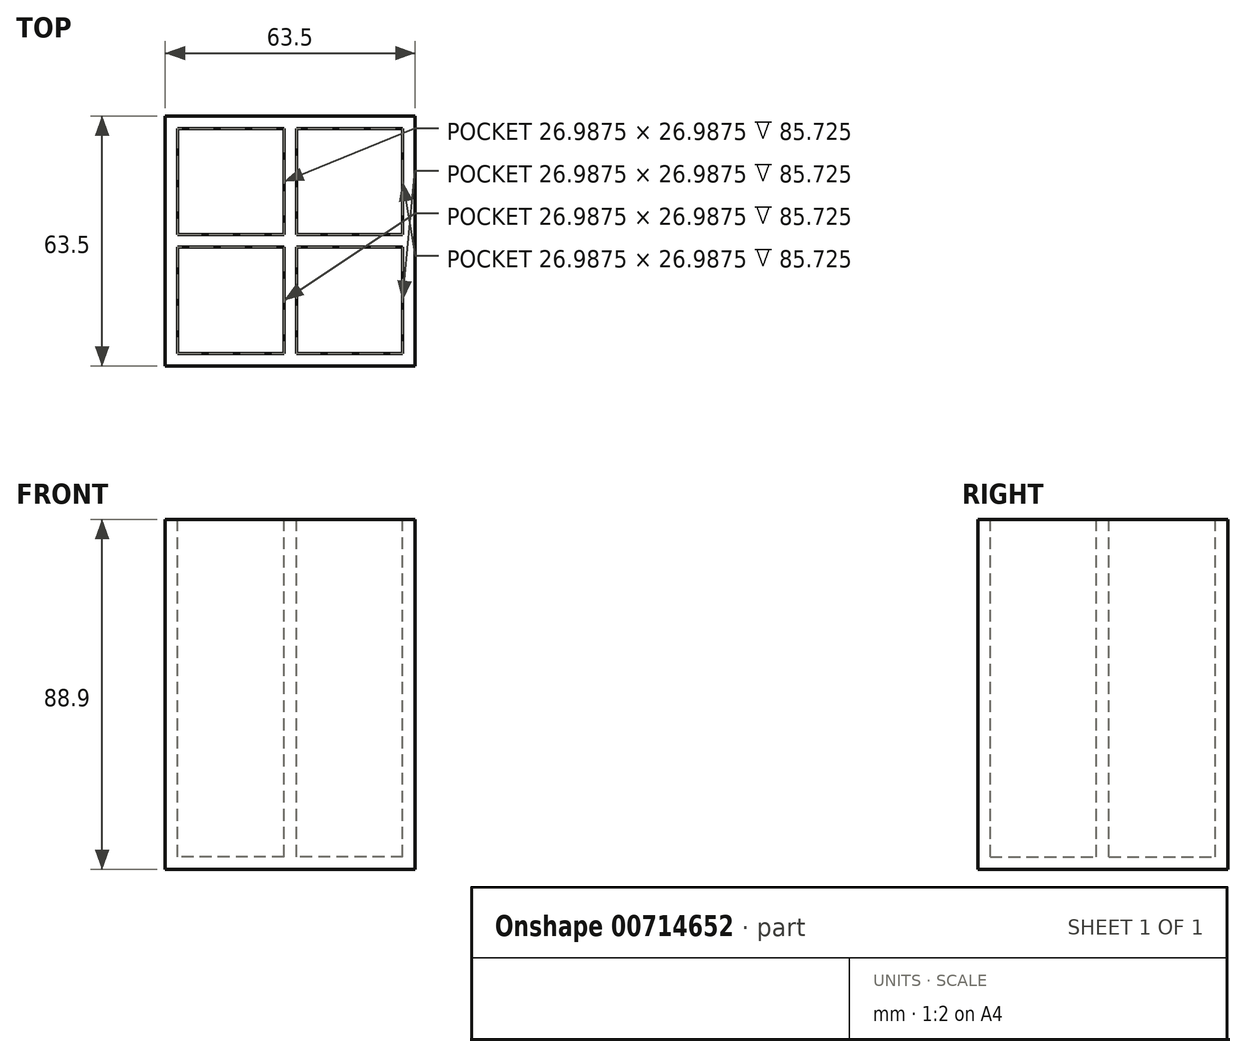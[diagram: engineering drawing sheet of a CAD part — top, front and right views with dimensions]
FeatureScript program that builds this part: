
annotation { "Feature Type Name" : "Feature", "Feature Type Description" : "" }
export const myFeature = defineFeature(function(context is Context, id is Id, definition is map)
    precondition{}
    {
        {
            var Q0;
            Q0=qCreatedBy(makeId("Top.planeOp"),FACE);
            var sketch = newSketch(context, id + "F0", { "sketchPlane" : qUnion([Q0])});
            skLineSegment(sketch, "E0.bottom", {"start": v(31.75, 31.75) * mm, "end": v(-31.75, 31.75) * mm});
            skLineSegment(sketch, "E0.top", {"start": v(31.75, -31.75) * mm, "end": v(-31.75, -31.75) * mm});
            skLineSegment(sketch, "E0.left", {"start": v(31.75, 31.75) * mm, "end": v(31.75, -31.75) * mm});
            skLineSegment(sketch, "E0.right", {"start": v(-31.75, 31.75) * mm, "end": v(-31.75, -31.75) * mm});
            skPoint(sketch, "E0.middle", {"position": v(0, 0) * mm});
            skSolve(sketch);
        }
        {
            var Q0;
            Q0 = qSketchRegion(id + "F0", true);
            extrude(context, id + "F1", {"entities" : qUnion([Q0]), "depth" : 88.9 * mm, "offsetDistance" : 25.4 * mm});
        }
        {
            var Q0;
            Q0=makeQuery(id+"F1.opExtrude","CAP_FACE",FACE,{"disambiguationData":[OSD([sQuery(id+"F0.wireOp",EDGE,"E0.bottom"),sQuery(id+"F0.wireOp",EDGE,"E0.top"),sQuery(id+"F0.wireOp",EDGE,"E0.left"),sQuery(id+"F0.wireOp",EDGE,"E0.right")])],"isStart":false});
            var sketch = newSketch(context, id + "F2", { "sketchPlane" : qUnion([Q0])});
            skLineSegment(sketch, "E1.bottom", {"start": v(-1.59, 1.59) * mm, "end": v(-28.57, 1.59) * mm});
            skLineSegment(sketch, "E1.top", {"start": v(-1.59, 28.58) * mm, "end": v(-28.58, 28.57) * mm});
            skLineSegment(sketch, "E1.left", {"start": v(-1.59, 1.59) * mm, "end": v(-1.59, 28.58) * mm});
            skLineSegment(sketch, "E1.right", {"start": v(-28.57, 1.59) * mm, "end": v(-28.58, 28.57) * mm});
            skPoint(sketch, "E1.middle", {"position": v(-15.08, 15.08) * mm});
            skLineSegment(sketch, "E2.bottom", {"start": v(28.57, 1.59) * mm, "end": v(1.59, 1.59) * mm});
            skLineSegment(sketch, "E2.top", {"start": v(28.58, 28.58) * mm, "end": v(1.59, 28.58) * mm});
            skLineSegment(sketch, "E2.left", {"start": v(28.58, 1.59) * mm, "end": v(28.58, 28.57) * mm});
            skLineSegment(sketch, "E2.right", {"start": v(1.59, 1.59) * mm, "end": v(1.59, 28.58) * mm});
            skPoint(sketch, "E2.middle", {"position": v(15.08, 15.08) * mm});
            skLineSegment(sketch, "E3.bottom", {"start": v(-1.59, -28.57) * mm, "end": v(-28.57, -28.58) * mm});
            skLineSegment(sketch, "E3.top", {"start": v(-1.59, -1.59) * mm, "end": v(-28.57, -1.59) * mm});
            skLineSegment(sketch, "E3.left", {"start": v(-1.59, -28.57) * mm, "end": v(-1.59, -1.59) * mm});
            skLineSegment(sketch, "E3.right", {"start": v(-28.57, -28.58) * mm, "end": v(-28.57, -1.59) * mm});
            skPoint(sketch, "E3.middle", {"position": v(-15.08, -15.08) * mm});
            skLineSegment(sketch, "E4.bottom", {"start": v(28.57, -28.57) * mm, "end": v(1.59, -28.57) * mm});
            skLineSegment(sketch, "E4.top", {"start": v(28.57, -1.59) * mm, "end": v(1.59, -1.59) * mm});
            skLineSegment(sketch, "E4.left", {"start": v(28.57, -28.57) * mm, "end": v(28.57, -1.59) * mm});
            skLineSegment(sketch, "E4.right", {"start": v(1.59, -28.58) * mm, "end": v(1.59, -1.59) * mm});
            skPoint(sketch, "E4.middle", {"position": v(15.08, -15.08) * mm});
            skSolve(sketch);
        }
        {
            var Q0;
            Q0 = qSketchRegion(id + "F2", true);
            extrude(context, id + "F3", {"entities" : qUnion([Q0]), "operationType" : NewBodyOperationType.REMOVE, "oppositeDirection" : true, "depth" : 85.72 * mm, "offsetDistance" : 25.4 * mm});
        }
    });
